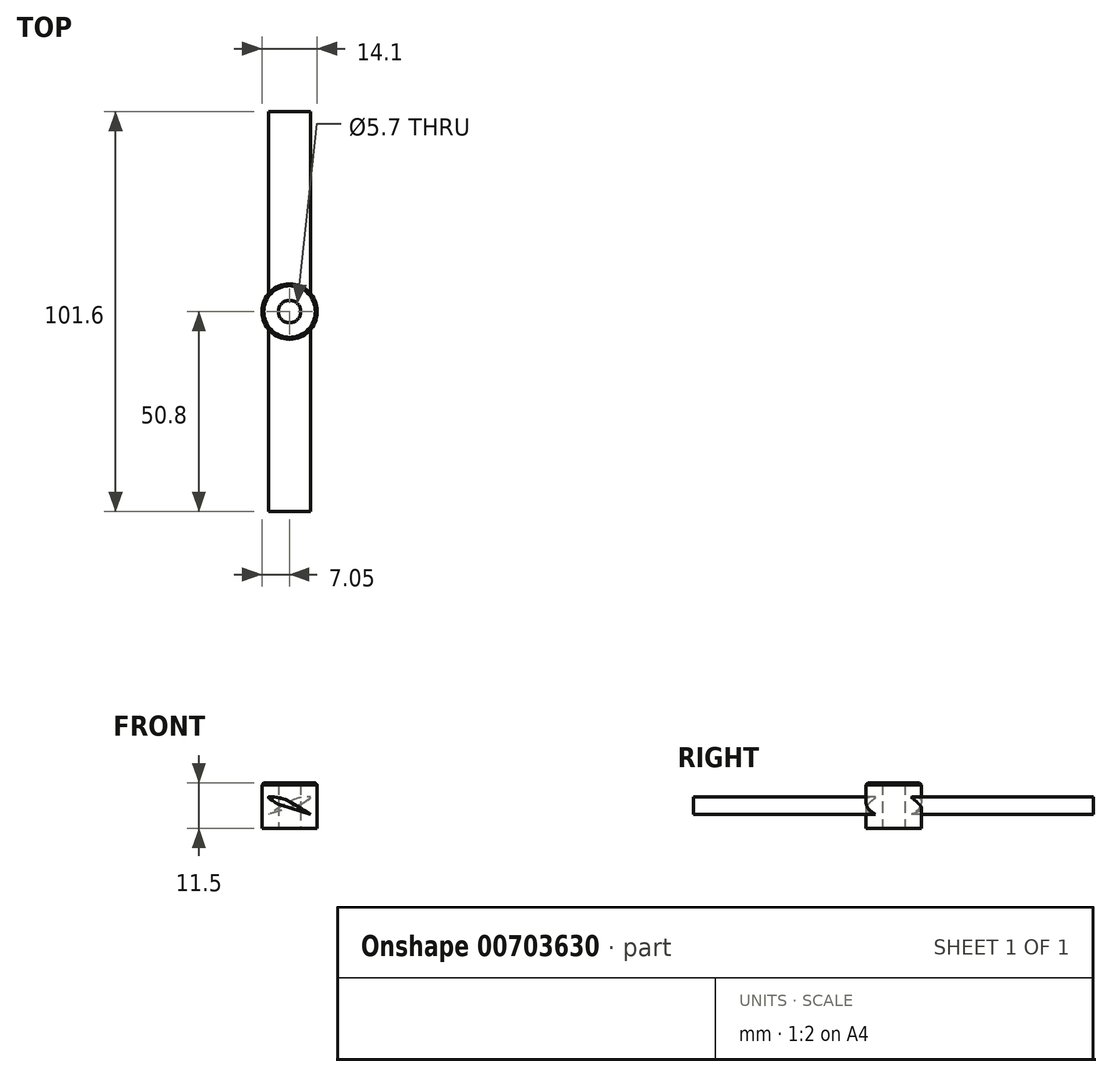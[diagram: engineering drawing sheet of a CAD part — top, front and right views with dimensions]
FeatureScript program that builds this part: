
annotation { "Feature Type Name" : "Feature", "Feature Type Description" : "" }
export const myFeature = defineFeature(function(context is Context, id is Id, definition is map)
    precondition{}
    {
        {
            var Q0;
            Q0=qCreatedBy(makeId("Top.planeOp"),FACE);
            var sketch = newSketch(context, id + "F0", { "sketchPlane" : qUnion([Q0])});
            skLineSegment(sketch, "E0", {"start": v(0, 0) * mm, "end": v(0, 50.8) * mm, "construction": true});
            skLineSegment(sketch, "E1", {"start": v(0, 0) * mm, "end": v(0, -50.8) * mm, "construction": true});
            skCircle(sketch, "E2", {"center": v(0, 0) * mm, "radius": 2.85 * mm});
            skCircle(sketch, "E3.0", {"center": v(0, 0) * mm, "radius": 7.05 * mm});
            skSolve(sketch);
        }
        {
            var Q0;
            Q0=makeQuery(id+"F0.imprint","IMPRINT",FACE,{"disambiguationData":[TD([[makeQuery(id+"F0.imprint","IMPRINT",EDGE,{"derivedFrom":sQuery(id+"F0.wireOp",EDGE,"E2")}),-1.0]])]});
            var Q1;
            Q1=makeQuery(id+"F0.imprint","IMPRINT",FACE,{"disambiguationData":[TD([[makeQuery(id+"F0.imprint","IMPRINT",EDGE,{"derivedFrom":sQuery(id+"F0.wireOp",EDGE,"E2")}),1.0]])]});
            extrude(context, id + "F1", {"entities" : qUnion([Q0, Q1]), "depth" : 11.5 * mm, "offsetDistance" : 25 * mm});
        }
        {
            var Q0;
            Q0=qCreatedBy(makeId("Front.planeOp"),FACE);
            var sketch = newSketch(context, id + "F2", { "sketchPlane" : qUnion([Q0])});
            skLineSegment(sketch, "E4", {"start": v(7.05, 6.9) * mm, "end": v(7.05, 0) * mm});
            skLineSegment(sketch, "E5", {"start": v(7.05, 0) * mm, "end": v(0, 0) * mm});
            skPoint(sketch, "E6", {"position": v(0, 5.75) * mm});
            skLineSegment(sketch, "E7", {"start": v(0, 0) * mm, "end": v(0, 11.5) * mm, "construction": true});
            skLineSegment(sketch, "E8.MirrorCS", {"start": v(-3.09, 6.17) * mm, "end": v(5.35, 3.59) * mm});
            skPoint(sketch, "E9.MirrorP", {"position": v(1.67, 4.7) * mm});
            skLineSegment(sketch, "E10.MirrorCS", {"start": v(0, 5.75) * mm, "end": v(-0.19, 5.28) * mm, "construction": true});
            skLineSegment(sketch, "E11.MirrorCS", {"start": v(0, 5.75) * mm, "end": v(0.34, 6.59) * mm, "construction": true});
            skLineSegment(sketch, "E12.MirrorCS", {"start": v(-5.35, 7.91) * mm, "end": v(5.35, 3.59) * mm, "construction": true});
            skFitSpline(sketch, "E13.MirrorCS", {"points": [v(-3.09, 6.17) * mm, v(-5.35, 7.91) * mm, v(-2.6, 7.75) * mm, v(-0.09, 6.82) * mm, v(2.63, 5.2) * mm, v(5.35, 3.59) * mm], "startDerivative": vector(-17.76, 12.97) * mm, "endDerivative": vector(12.95, -7.56) * mm});
            skLineSegment(sketch, "E14.MirrorCS", {"start": v(2.41, 4.49) * mm, "end": v(2.63, 5.2) * mm, "construction": true});
            skLineSegment(sketch, "E15.MirrorCS", {"start": v(-0.53, 5.39) * mm, "end": v(-0.09, 6.82) * mm, "construction": true});
            skLineSegment(sketch, "E16.MirrorCS", {"start": v(-5.64, 6.96) * mm, "end": v(-5.35, 7.91) * mm, "construction": true});
            skLineSegment(sketch, "E17.MirrorCS", {"start": v(-3.09, 6.17) * mm, "end": v(-2.6, 7.75) * mm, "construction": true});
            skLineSegment(sketch, "E18.MirrorCS", {"start": v(-0.53, 5.39) * mm, "end": v(5.35, 3.59) * mm, "construction": true});
            skLineSegment(sketch, "E19.MirrorCS", {"start": v(-0.53, 5.39) * mm, "end": v(-5.64, 6.96) * mm, "construction": true});
            skPoint(sketch, "E20.MirrorP", {"position": v(-1.99, 7.45) * mm});
            skSolve(sketch);
        }
        {
            var Q0;
            Q0=makeQuery(id+"F2.imprint","IMPRINT",FACE,{"disambiguationData":[TD([[makeQuery(id+"F2.imprint","IMPRINT",EDGE,{"derivedFrom":sQuery(id+"F2.wireOp",EDGE,"E8.MirrorCS")}),1.0]])]});
            extrude(context, id + "F3", {"entities" : qUnion([Q0]), "operationType" : NewBodyOperationType.ADD, "depth" : 50.8 * mm, "offsetDistance" : 25 * mm});
        }
        {
            var Q0;
            {var subQ0=sQuery(id+"F2.wireOp",EDGE,"msobF1Sl-cq8Q-FyCY-6Z0W-24ijWpGXxMAd");var subQ1=sQuery(id+"F2.wireOp",EDGE,"6ce1abe7-e2ef-4290-bca9-f703ce693d8b");Q0=makeQuery(id+"F3.opExtrude","SWEPT_EDGE",EDGE,{"disambiguationData":[OSD([subQ1,subQ0]),TDD([makeQuery(id+"F2.imprint","INTERSECT",VERTEX,{"disambiguationData":[OD(0.0)],"derivedFrom":[subQ1,subQ0]})])]});}
            var Q1;
            {var subQ0=sQuery(id+"F2.wireOp",EDGE,"E13.MirrorCS");var subQ1=sQuery(id+"F2.wireOp",EDGE,"E8.MirrorCS");Q1=makeQuery(id+"F3.opExtrude","SWEPT_EDGE",EDGE,{"disambiguationData":[OSD([subQ1,subQ0]),TDD([makeQuery(id+"F2.imprint","INTERSECT",VERTEX,{"disambiguationData":[OD(0.0)],"derivedFrom":[subQ1,subQ0]})])]});}
            fillet(context, id + "F4", {"entities" : qUnion([Q0, Q1]), "radius" : 5 * mm, "tangentPropagation" : true, "allowEdgeOverflow" : false});
        }
        {
            var Q0;
            Q0=qCreatedBy(makeId("Front.planeOp"),FACE);
            var sketch = newSketch(context, id + "F5", { "sketchPlane" : qUnion([Q0])});
            skLineSegment(sketch, "E21", {"start": v(7.05, 6.9) * mm, "end": v(7.05, 0) * mm});
            skLineSegment(sketch, "E22", {"start": v(7.05, 0) * mm, "end": v(0, 0) * mm});
            skLineSegment(sketch, "E23", {"start": v(7.05, 4.07) * mm, "end": v(7.05, 0) * mm});
            skLineSegment(sketch, "E24", {"start": v(7.05, 3.95) * mm, "end": v(7.05, 5.45) * mm});
            skLineSegment(sketch, "E25", {"start": v(7.05, 4.95) * mm, "end": v(7.05, 3.75) * mm});
            skPoint(sketch, "E26.endSnap0", {"position": v(7.05, 2.04) * mm});
            skPoint(sketch, "E27", {"position": v(0, 5.75) * mm});
            skLineSegment(sketch, "E28", {"start": v(0, 0) * mm, "end": v(0, 11.5) * mm, "construction": true});
            skPoint(sketch, "E29.MirrorP", {"position": v(-1.67, 4.7) * mm});
            skLineSegment(sketch, "E30.MirrorCS", {"start": v(3.09, 6.17) * mm, "end": v(-5.35, 3.59) * mm});
            skLineSegment(sketch, "E31.MirrorCS", {"start": v(0, 5.75) * mm, "end": v(-0.34, 6.59) * mm, "construction": true});
            skLineSegment(sketch, "E32.MirrorCS", {"start": v(0, 5.75) * mm, "end": v(0.19, 5.28) * mm, "construction": true});
            skLineSegment(sketch, "E33.MirrorCS", {"start": v(0.53, 5.39) * mm, "end": v(0.09, 6.82) * mm, "construction": true});
            skLineSegment(sketch, "E34.MirrorCS", {"start": v(3.09, 6.17) * mm, "end": v(2.6, 7.75) * mm, "construction": true});
            skLineSegment(sketch, "E35.MirrorCS", {"start": v(-2.41, 4.49) * mm, "end": v(-2.63, 5.2) * mm, "construction": true});
            skLineSegment(sketch, "E36.MirrorCS", {"start": v(0.53, 5.39) * mm, "end": v(-5.35, 3.59) * mm, "construction": true});
            skLineSegment(sketch, "E37.MirrorCS", {"start": v(0.53, 5.39) * mm, "end": v(5.64, 6.96) * mm, "construction": true});
            skLineSegment(sketch, "E38.MirrorCS", {"start": v(5.35, 7.91) * mm, "end": v(-5.35, 3.59) * mm, "construction": true});
            skLineSegment(sketch, "E39.MirrorCS", {"start": v(5.64, 6.96) * mm, "end": v(5.35, 7.91) * mm, "construction": true});
            skFitSpline(sketch, "E40.MirrorCS", {"points": [v(3.09, 6.17) * mm, v(5.35, 7.91) * mm, v(2.6, 7.75) * mm, v(0.09, 6.82) * mm, v(-2.63, 5.2) * mm, v(-5.35, 3.59) * mm], "startDerivative": vector(17.76, 12.97) * mm, "endDerivative": vector(-12.95, -7.56) * mm});
            skSolve(sketch);
        }
        {
            var Q0;
            Q0=makeQuery(id+"F5.imprint","IMPRINT",FACE,{"disambiguationData":[TD([[makeQuery(id+"F5.imprint","IMPRINT",EDGE,{"derivedFrom":sQuery(id+"F5.wireOp",EDGE,"E30.MirrorCS")}),-1.0]])]});
            extrude(context, id + "F6", {"entities" : qUnion([Q0]), "operationType" : NewBodyOperationType.ADD, "oppositeDirection" : true, "depth" : 50.8 * mm, "offsetDistance" : 25 * mm});
        }
        {
            var Q0;
            {var subQ0=sQuery(id+"Fv6gQINzxOytYec_1.wireOp",EDGE,"d878019e-00ca-4c95-9281-a5dbebea3d630.MirrorCS");var subQ1=sQuery(id+"Fv6gQINzxOytYec_1.wireOp",EDGE,"19222e45-0a99-4dbb-b0f8-06b7d0d080b00.MirrorCS");Q0=makeQuery(id+"F6.opExtrude","SWEPT_EDGE",EDGE,{"disambiguationData":[OSD([subQ1,subQ0]),TDD([makeQuery(id+"Fv6gQINzxOytYec_1.imprint","INTERSECT",VERTEX,{"disambiguationData":[OD(0.0)],"derivedFrom":[subQ1,subQ0]})])]});}
            var Q1;
            {var subQ0=sQuery(id+"Fj0TBoSZPlOelra_1.wireOp",EDGE,"c5e6d0e3-df62-49b4-9d73-401119eaf40d2.MirrorCS");var subQ1=sQuery(id+"Fj0TBoSZPlOelra_1.wireOp",EDGE,"c5e6d0e3-df62-49b4-9d73-401119eaf40d1.MirrorCS");Q1=makeQuery(id+"F6.opExtrude","SWEPT_EDGE",EDGE,{"disambiguationData":[OSD([subQ1,subQ0]),TDD([makeQuery(id+"Fj0TBoSZPlOelra_1.imprint","INTERSECT",VERTEX,{"disambiguationData":[OD(0.0)],"derivedFrom":[subQ1,subQ0]})])]});}
            var Q2;
            {var subQ0=sQuery(id+"F5.wireOp",EDGE,"f684c9b4-9527-4a63-8f31-0619753b8ec57.MirrorCS");var subQ1=sQuery(id+"F5.wireOp",EDGE,"f684c9b4-9527-4a63-8f31-0619753b8ec52.MirrorCS");Q2=makeQuery(id+"F6.opExtrude","SWEPT_EDGE",EDGE,{"disambiguationData":[OSD([subQ1,subQ0]),TDD([makeQuery(id+"F5.imprint","INTERSECT",VERTEX,{"disambiguationData":[OD(0.0)],"derivedFrom":[subQ1,subQ0]})])]});}
            var Q3;
            {var subQ0=sQuery(id+"F5.wireOp",EDGE,"E40.MirrorCS");var subQ1=sQuery(id+"F5.wireOp",EDGE,"E30.MirrorCS");Q3=makeQuery(id+"F6.opExtrude","SWEPT_EDGE",EDGE,{"disambiguationData":[OSD([subQ1,subQ0]),TDD([makeQuery(id+"F5.imprint","INTERSECT",VERTEX,{"disambiguationData":[OD(0.0)],"derivedFrom":[subQ1,subQ0]})])]});}
            fillet(context, id + "F7", {"entities" : qUnion([Q0, Q1, Q2, Q3]), "radius" : 5 * mm, "tangentPropagation" : true, "allowEdgeOverflow" : false});
        }
        {
            var Q0;
            Q0=makeQuery(id+"F0.imprint","IMPRINT",FACE,{"disambiguationData":[TD([[makeQuery(id+"F0.imprint","IMPRINT",EDGE,{"derivedFrom":sQuery(id+"F0.wireOp",EDGE,"E2")}),1.0]])]});
            extrude(context, id + "F8", {"entities" : qUnion([Q0]), "operationType" : NewBodyOperationType.REMOVE, "depth" : 25 * mm, "offsetDistance" : 25 * mm});
        }
        {
            var Q0;
            Q0=makeQuery(id+"F1.opExtrude","CAP_EDGE",EDGE,{"disambiguationData":[OSD([sQuery(id+"F0.wireOp",EDGE,"E3.0")])],"isStart":false});
            chamfer(context, id + "F9", {"entities" : qUnion([Q0]), "width" : .5 * mm, "tangentPropagation" : true});
        }
    });
